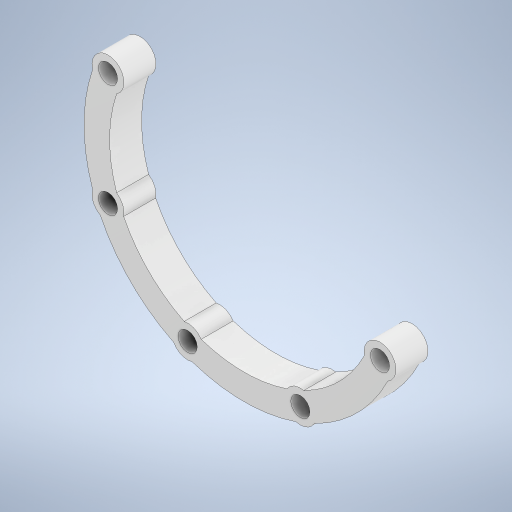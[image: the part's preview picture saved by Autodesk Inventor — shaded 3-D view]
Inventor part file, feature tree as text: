
AUTODESK INVENTOR PART (.ipt)
format: ipt  version: 2024.3 (Build 283343000, 343)  size: 344,064 bytes
history: native  units: mm
features: extrude x2, sketch x2, other x1, projected_geometry x1
ambient origin geometry x8: Origin, YZ Plane, XZ Plane, XY Plane, X Axis, Y Axis, Z Axis, Center Point
bodies: Body1 (feature_tree)
feature tree (6):
  other  "ソリッド1"
  extrude  "押し出し1"  Depth=92.0mm
  extrude  "押し出し2"  Depth=100.0mm
  sketch  "スケッチ1"
  sketch  "スケッチ2"
  projected_geometry  "投影ループ1"
